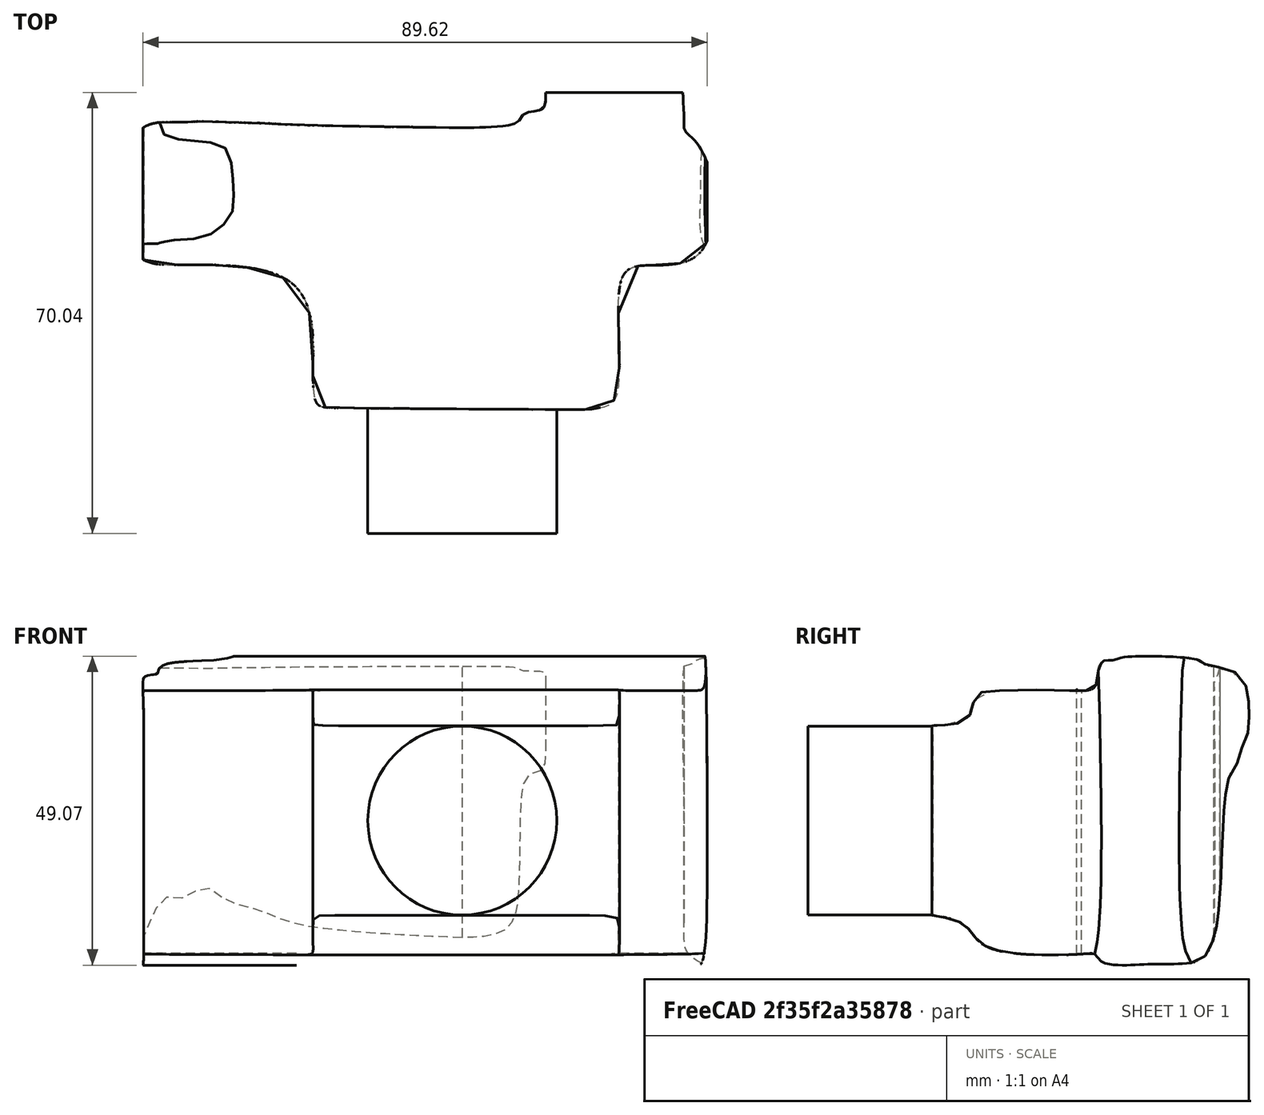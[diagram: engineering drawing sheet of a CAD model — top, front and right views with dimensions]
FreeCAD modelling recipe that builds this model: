
FCSTD DOCUMENT  (FreeCAD 0.18R14555 (Git shallow))
Label: camera
License: All rights reserved
LicenseURL: http://en.wikipedia.org/wiki/All_rights_reserved
objects: Image::ImagePlane×3, Sketcher::SketchObject×3, Part::Extrusion×3, Part::MultiCommon×1, Part::Cylinder×1, Part::MultiFuse×1
note: 9 computed .brp shape members not serialized (recipe doc carries the construction recipe); baked Part::Feature solids carry a one-line shape summary decoded from their .brp

FEATURE [Image::ImagePlane] ImagePlane  label="TopPlane"
  Placement = pos=(-7,0,0) rot=(0,0,1;3.14159rad)
  XSize = 111
  YSize = 61
FEATURE [Image::ImagePlane] ImagePlane002  label="FrontPlane"
  Placement = pos=(-5,2,4e-16) rot=(1,0,0;1.5708rad)
  XSize = 107
  YSize = 60
FEATURE [Sketcher::SketchObject] Sketch  label="Top View"
  sketch-geometry (107):
    g0-g53: Circle [constr] x54 (B-spline internal-alignment scaffolding for g54; pole/knot coordinates omitted)
    g54: BSplineCurve PolesCount=54 KnotsCount=52 Degree=3 IsPeriodic=0
    g55-g106: GeomPoint [constr] x52 (B-spline internal-alignment scaffolding for g54; pole/knot coordinates omitted)
  constraints (10):
    c: PointOnObject(g54,g-2)
    c: Radius(g0) = 1
    c: Equal(g0, g1-g27) x27
    c: PointOnObject(g27,g26)
    c: Equal(g0, g28-g32) x5
    c: PointOnObject(g32,g31)
    c: Equal(g0, g33-g53) x21
    c: Coincident(g53,g0)
    c: InternalAlignment(g0-g53 -> g54) x54
    c: InternalAlignment(g55-g106 -> g54) x52
FEATURE [Sketcher::SketchObject] Sketch001  label="Front View"
  Placement = pos=(0,0,0) rot=(1,0,0;1.5708rad)
  sketch-geometry (49):
    g0-g24: Circle [constr] x25 (B-spline internal-alignment scaffolding for g25; pole/knot coordinates omitted)
    g25: BSplineCurve PolesCount=25 KnotsCount=23 Degree=3 IsPeriodic=0
    g26-g48: GeomPoint [constr] x23 (B-spline internal-alignment scaffolding for g25; pole/knot coordinates omitted)
  constraints (5):
    c: Radius(g0) = 6
    c: Equal(g0, g1-g24) x24
    c: Coincident(g24,g0)
    c: InternalAlignment(g0-g24 -> g25) x25
    c: InternalAlignment(g26-g48 -> g25) x23
FEATURE [Image::ImagePlane] ImagePlane003  label="SidePlane"
  Placement = pos=(2,-11,0) rot=(0.57735,0.57735,0.57735;2.0944rad)
  XSize = 82
  YSize = 60
FEATURE [Sketcher::SketchObject] Sketch002  label="Side View"
  Placement = pos=(0,0,0) rot=(0.57735,-0.57735,-0.57735;2.0944rad)
  sketch-geometry (91):
    g0-g45: Circle [constr] x46 (B-spline internal-alignment scaffolding for g46; pole/knot coordinates omitted)
    g46: BSplineCurve PolesCount=46 KnotsCount=44 Degree=3 IsPeriodic=0
    g47-g90: GeomPoint [constr] x44 (B-spline internal-alignment scaffolding for g46; pole/knot coordinates omitted)
  constraints (14):
    c: PointOnObject(g46,g-1)
    c: Radius(g0) = 1
    c: Equal(g0, g1-g15) x15
    c: PointOnObject(g15,g-2)
    c: Equal(g0,g16)
    c: PointOnObject(g16,g-2)
    c: Equal(g0, g17-g35) x19
    c: PointOnObject(g35,g-2)
    c: Equal(g0,g36)
    c: PointOnObject(g36,g-2)
    c: Equal(g0, g37-g45) x9
    c: Coincident(g45,g0)
    c: InternalAlignment(g0-g45 -> g46) x46
    c: InternalAlignment(g47-g90 -> g46) x44
FEATURE [Part::Extrusion] Extrude
  Base = -> Sketch
  Dir = (0,0,1)
  DirMode = 2
  FaceMakerClass = Part::FaceMakerBullseye
  LengthFwd = 200
  LengthRev = 0
  Solid = true
  Symmetric = true
FEATURE [Part::Extrusion] Extrude001
  Base = -> Sketch001
  Dir = (0,-1,0)
  DirMode = 2
  FaceMakerClass = Part::FaceMakerBullseye
  LengthFwd = 200
  LengthRev = 0
  Solid = true
  Symmetric = true
FEATURE [Part::Extrusion] Extrude002
  Base = -> Sketch002
  Dir = (-1,0,0)
  DirMode = 2
  FaceMakerClass = Part::FaceMakerBullseye
  LengthFwd = 200
  LengthRev = 0
  Solid = true
  Symmetric = true
FEATURE [Part::MultiCommon] Common
  Shapes = -> [Extrude,Extrude001,Extrude002]
FEATURE [Part::Cylinder] Cylinder
  Angle = 360
  AttacherType = Attacher::AttachEngine3D
  Height = 25
  Placement = pos=(0,-21,-3) rot=(1,0,0;1.5708rad)
  Radius = 15
FEATURE [Part::MultiFuse] Fusion
  Shapes = -> [Cylinder,Common]
